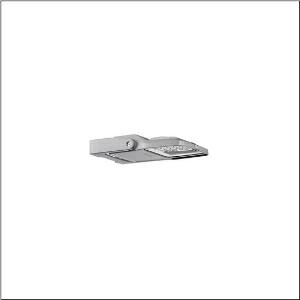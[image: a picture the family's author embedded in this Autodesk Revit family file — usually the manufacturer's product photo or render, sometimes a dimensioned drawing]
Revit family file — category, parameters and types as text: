
# Revit family: floodlight_fl_21_iq_micro___pl61_5xa7761a2c2a_8a4e
name_source: partatom
category: Lighting Fixtures
units: mm (PartAtom-declared; Revit-internal decimal feet)

## family parameters
Cut with Voids When Loaded = No
Host = Face
Light Source = No
Part Type = Normal
Room Calculation Point = No
Round Connector Dimension = Use Diameter
Shared = No

## types (1)
- --- (1 x LED, 2910 lm, 23.1 W, 3000K)
    Apparent Load = 23 VA
    CIE Flux Codes = 33 65 98 100 100
    Color Rendering = 70
    Color Temperature = 3000K
    Default Elevation = 1800 mm
    Description = Floodlight FL 21 iQ micro, floodlight, primary light control with lens, of PMMA, primary optical cover: protective disc, of toughened safety glass, transparent, light distribution: PL61, light emission: direct distribution, installation type: surface-mounted, LED, High Power LED, rated luminous flux: 2.910lm, luminous efficacy: 126lm/W, light colour: 730, colour temperature: 3000K, control: optimised constant luminous flux control (CLO 2.0), Desk-Remote (wireless, voltage-free reading and setting of iQ features in the workshop via application-optimized NFC function/RFID function), Light-Fading, Smart-Wire, Night-Set, Lumen-Switch, Temp-Guard, Auto-Match, with terminal, 6-pole, mains connection: 220..240V, AC, 50/60Hz, start of lifetime: 23W, end of service life: 24W, reduction: 11W, luminaire housing, of diecast aluminium, powder-coated, Siteco® metallic grey (DB 702S), corrosivity category C5 mid according to DIN EN ISO 12944, sealing non-destructively replaceable, design bracket, of diecast aluminium, powder-coated, Siteco® metallic grey (DB 702S), protection rating (complete): IP66, insulation class (complete): insulation class II (safety insulation), certification: CE, ENEC, VDE, protection symbol: D, impact resistance: IK07, permissible operating ambient temperature: -40..+40°C, permissible operating ambient temperature for outdoor applications: -40..+50°C, standard: DIN EN 12944, LABS conformity tested according to VDMA 24364:2018-05, packaging unit: 1 piece

Light Distribution: PL61
    Height = 65 mm
    Lamp = 1 x LED
    Lamp Light Flux = 2910 lm
    Lamp Power = 23.1 W
    Lamp count = 1
    Length = 312 mm
    Luminous efficacy = 126 lm/W
    Manufacturer = Siteco
    ModVariant = No
    Model = 5XA7761A2C2A
    Mounting Place = Wall
    Mounting Type = Surface mounted
    Number of Poles = 1
    OnlyDefault = Yes
    Power Factor = 1
    Product Name = Floodlight FL 21 iQ micro | PL61
    Product group = floodlight | wall mounted
    ProductGroupID = 2001
    Protection Class = Protection class II
    Protection Degree = IP 66
    RLX_Detail_Level = 1
    RLX_Emergency_Light_Flux = 0 lm
    RLX_Emergency_Type = 0
    RLX_Emergency_Type_DB = No
    RlxData = <blob elided: 97937 chars, md5=f33a9d97>
    Socket = socket
    Standby Power = 0 W
    System Light Flux = 2910 lm
    System Power = 23 W
    Type Comments = factory setting: luminous flux: 100 % | dim-lin: 254 | 455 mA
    Type Image = l_1006878.jpg
    URL = http://relux.com
    VarID = @adj_147301
    Voltage = 0 V
    Weight = 0.00 kg
    Width = 230 mm

## geometry (parser evidence)
native form markers: Blend x4, Sweep x13
no freeform markers — native parametric forms only
